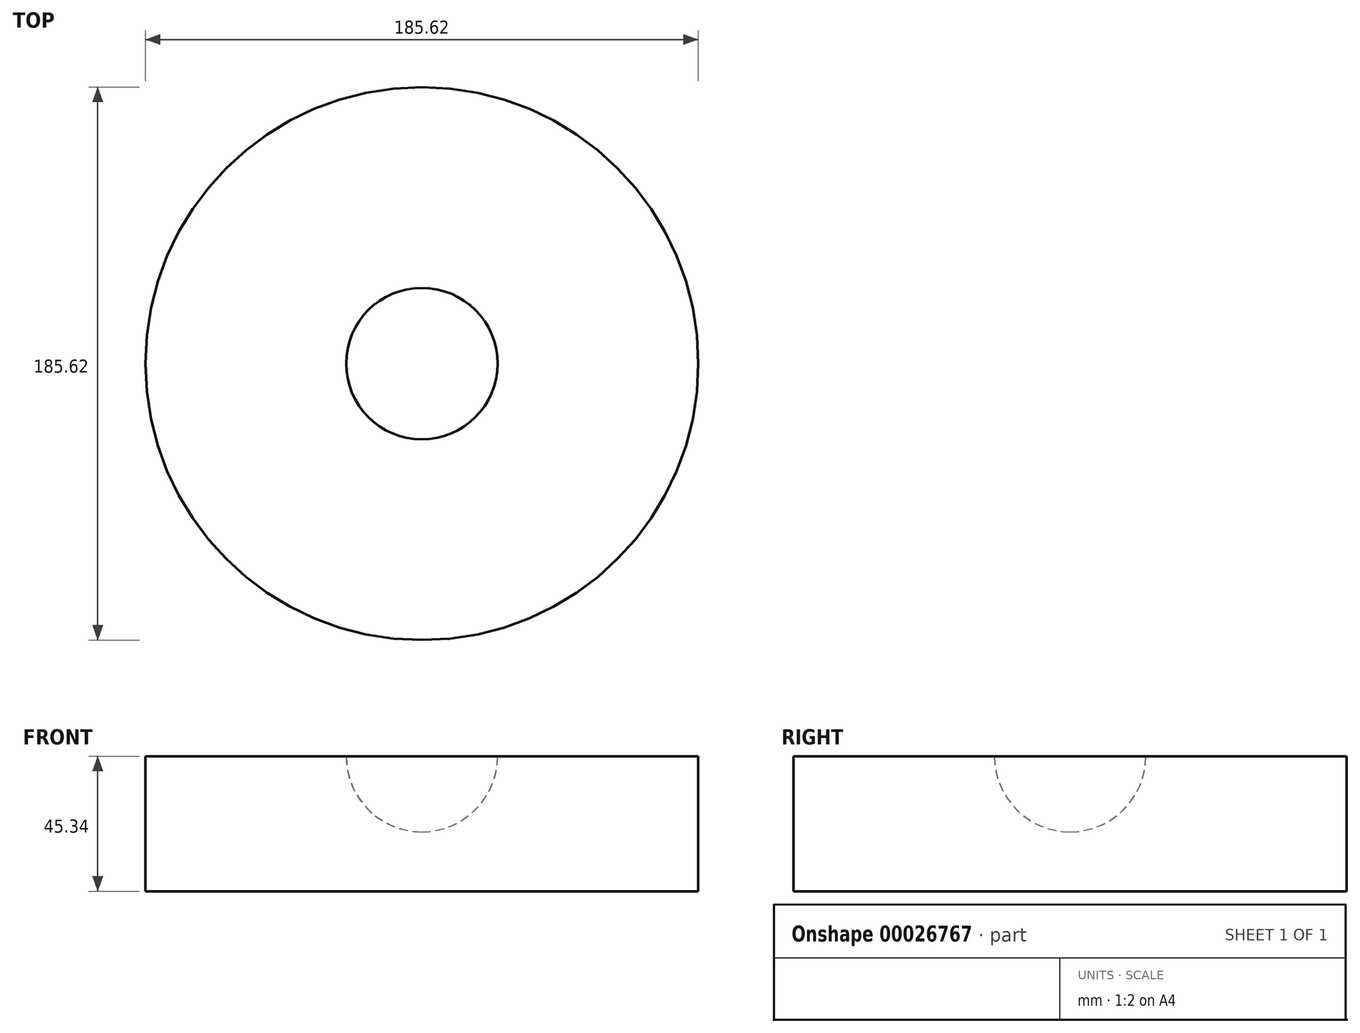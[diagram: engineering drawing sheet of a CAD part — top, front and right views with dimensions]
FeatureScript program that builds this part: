
annotation { "Feature Type Name" : "Feature", "Feature Type Description" : "" }
export const myFeature = defineFeature(function(context is Context, id is Id, definition is map)
    precondition{}
    {
        {
            var Q0;
            Q0=qCreatedBy(makeId("Front.planeOp"),FACE);
            var sketch = newSketch(context, id + "F0", { "sketchPlane" : qUnion([Q0])});
            skArc(sketch, "E0", {"start": v(0, -25.4) * mm, "mid": v(17.96, -17.96) * mm, "end": v(25.4, 0) * mm});
            skPoint(sketch, "E1", {"position": v(25.4, 0) * mm});
            skPoint(sketch, "E2", {"position": v(0, -25.4) * mm});
            skLineSegment(sketch, "E3", {"start": v(25.4, 0) * mm, "end": v(92.8, 0) * mm});
            skLineSegment(sketch, "E4", {"start": v(92.8, 0) * mm, "end": v(92.8, -45.34) * mm});
            skLineSegment(sketch, "E5", {"start": v(92.8, -45.34) * mm, "end": v(0, -45.34) * mm});
            skLineSegment(sketch, "E6", {"start": v(0, -45.34) * mm, "end": v(0, -25.4) * mm});
            skSolve(sketch);
        }
        {
            var Q0;
            Q0=makeQuery(id+"F0.imprint","IMPRINT",FACE,{"disambiguationData":[TD([[makeQuery(id+"F0.imprint","IMPRINT",EDGE,{"derivedFrom":sQuery(id+"F0.wireOp",EDGE,"E0")}),-1.0]])]});
            var Q1;
            Q1=sQuery(id+"F0.wireOp",EDGE,"E6");
            revolve(context, id + "F1", {"entities" : qUnion([Q0]), "axis" : qUnion([Q1]), "revolveType" : RevolveType.FULL});
        }
    });
